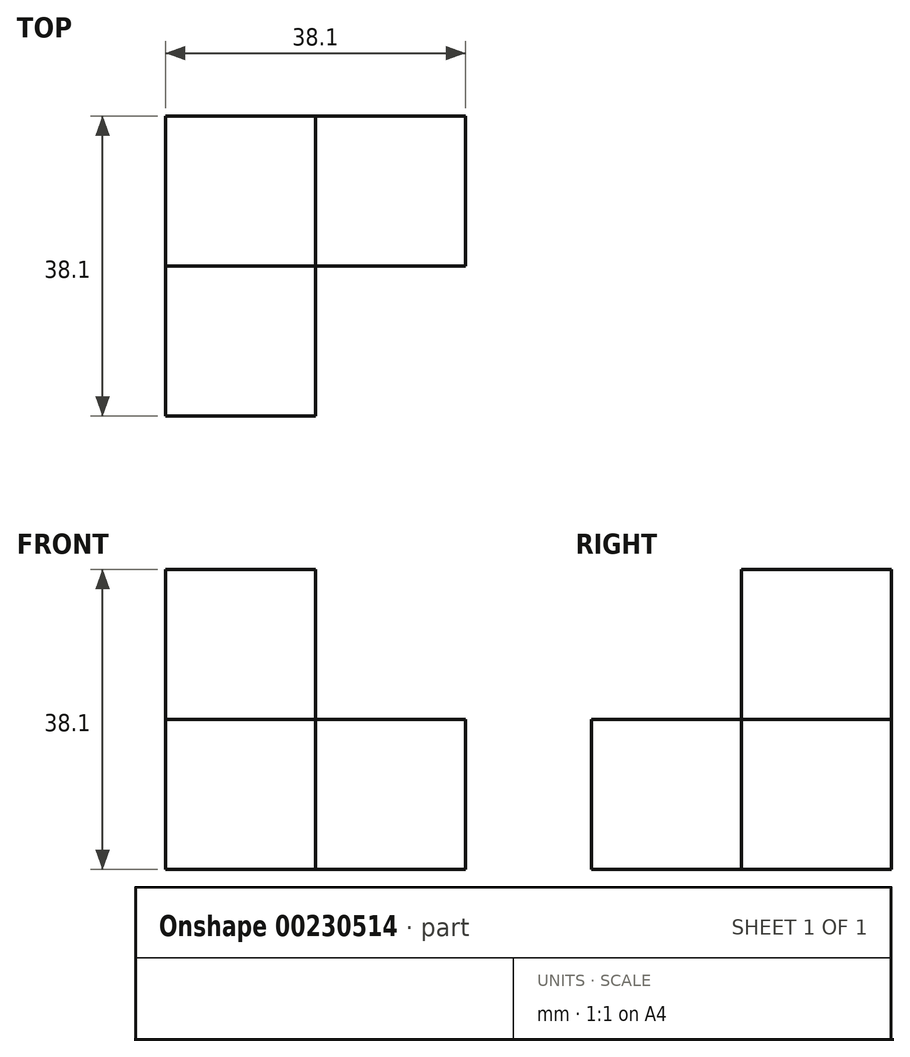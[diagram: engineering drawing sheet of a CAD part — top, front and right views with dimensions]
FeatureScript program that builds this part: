
annotation { "Feature Type Name" : "Feature", "Feature Type Description" : "" }
export const myFeature = defineFeature(function(context is Context, id is Id, definition is map)
    precondition{}
    {
        {
            var Q0;
            Q0=qCreatedBy(makeId("Top.planeOp"),FACE);
            var sketch = newSketch(context, id + "F0", { "sketchPlane" : qUnion([Q0])});
            skLineSegment(sketch, "E0", {"start": v(0, 0) * mm, "end": v(0, 38.1) * mm});
            skLineSegment(sketch, "E1", {"start": v(0, 38.1) * mm, "end": v(38.1, 38.1) * mm});
            skLineSegment(sketch, "E2", {"start": v(38.1, 38.1) * mm, "end": v(38.1, 19.05) * mm});
            skLineSegment(sketch, "E3", {"start": v(38.1, 19.05) * mm, "end": v(19.05, 19.05) * mm});
            skLineSegment(sketch, "E4", {"start": v(19.05, 19.05) * mm, "end": v(19.05, 0) * mm});
            skLineSegment(sketch, "E5", {"start": v(19.05, 0) * mm, "end": v(0, 0) * mm});
            skPoint(sketch, "E6.start.orphan", {"position": v(0, 19.05) * mm});
            skPoint(sketch, "E7.end.orphan", {"position": v(19.05, 38.1) * mm});
            skSolve(sketch);
        }
        {
            var Q0;
            Q0=makeQuery(id+"F0.imprint","IMPRINT",FACE,{"disambiguationData":[TD([[makeQuery(id+"F0.imprint","IMPRINT",EDGE,{"derivedFrom":sQuery(id+"F0.wireOp",EDGE,"E0")}),-1.0]])]});
            extrude(context, id + "F1", {"entities" : qUnion([Q0]), "depth" : 19.05 * mm});
        }
        {
            var Q0;
            Q0=makeQuery(id+"F1.opExtrude","CAP_FACE",FACE,{"disambiguationData":[OSD([sQuery(id+"F0.wireOp",EDGE,"E0"),sQuery(id+"F0.wireOp",EDGE,"E1"),sQuery(id+"F0.wireOp",EDGE,"E2"),sQuery(id+"F0.wireOp",EDGE,"E3"),sQuery(id+"F0.wireOp",EDGE,"E4"),sQuery(id+"F0.wireOp",EDGE,"E5")])],"isStart":false});
            var sketch = newSketch(context, id + "F2", { "sketchPlane" : qUnion([Q0])});
            skLineSegment(sketch, "E8.bottom", {"start": v(0, 38.1) * mm, "end": v(19.05, 38.1) * mm});
            skLineSegment(sketch, "E8.top", {"start": v(0, 19.05) * mm, "end": v(19.05, 19.05) * mm});
            skLineSegment(sketch, "E8.left", {"start": v(0, 38.1) * mm, "end": v(0, 19.05) * mm});
            skLineSegment(sketch, "E8.right", {"start": v(19.05, 38.1) * mm, "end": v(19.05, 19.05) * mm});
            skSolve(sketch);
        }
        {
            var Q0;
            Q0=makeQuery(id+"F2.imprint","IMPRINT",FACE,{"disambiguationData":[TD([[makeQuery(id+"F2.imprint","IMPRINT",EDGE,{"derivedFrom":sQuery(id+"F2.wireOp",EDGE,"E8.bottom")}),-1.0]])]});
            extrude(context, id + "F3", {"entities" : qUnion([Q0]), "operationType" : NewBodyOperationType.ADD, "depth" : 19.05 * mm});
        }
    });
